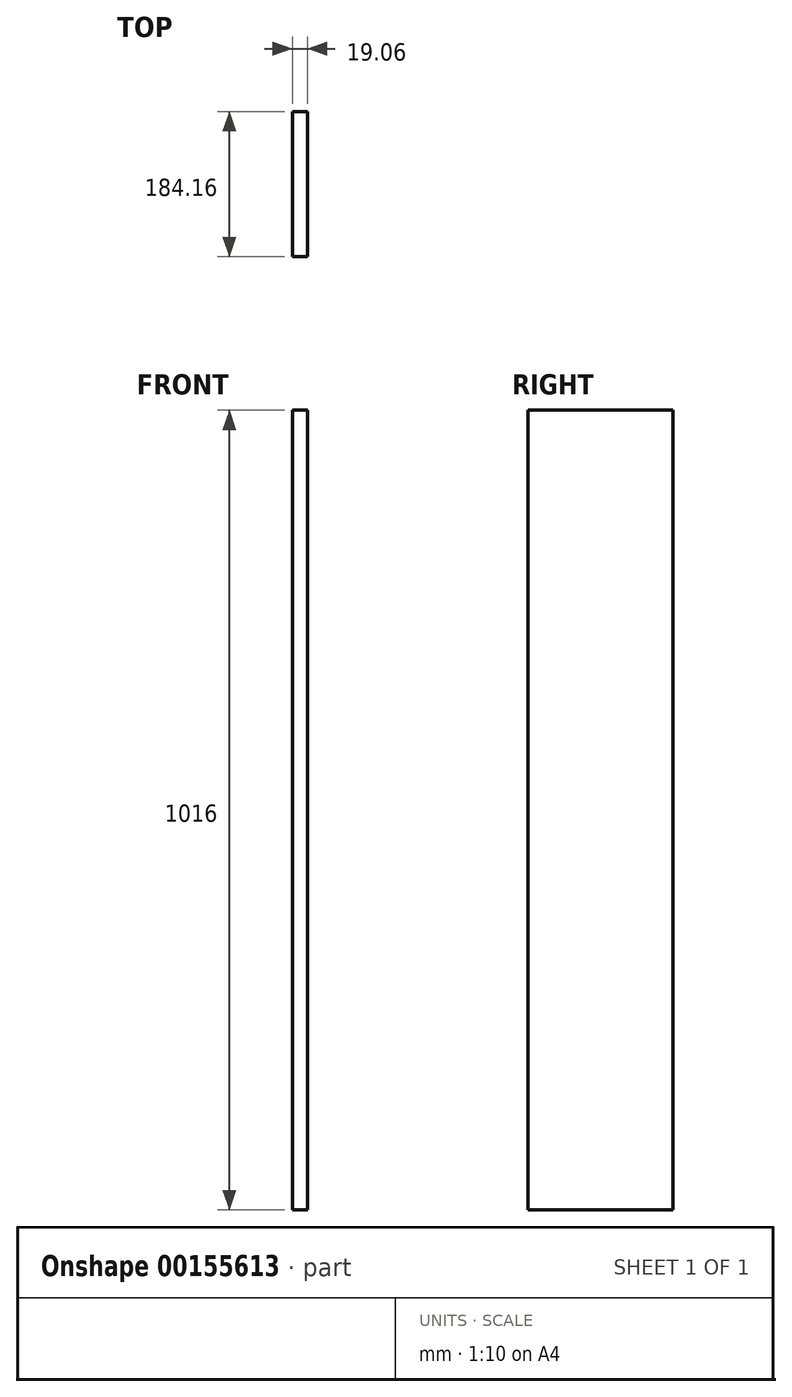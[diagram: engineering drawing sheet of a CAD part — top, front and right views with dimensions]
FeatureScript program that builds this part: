
annotation { "Feature Type Name" : "Feature", "Feature Type Description" : "" }
export const myFeature = defineFeature(function(context is Context, id is Id, definition is map)
    precondition{}
    {
        {
            var Q0;
            Q0=qCreatedBy(makeId("Top.planeOp"),FACE);
            var sketch = newSketch(context, id + "F0", { "sketchPlane" : qUnion([Q0])});
            skLineSegment(sketch, "E0.bottom", {"start": v(-9.53, 92.08) * mm, "end": v(9.52, 92.08) * mm});
            skLineSegment(sketch, "E0.top", {"start": v(-9.53, -92.08) * mm, "end": v(9.52, -92.08) * mm});
            skLineSegment(sketch, "E0.left", {"start": v(-9.53, 92.07) * mm, "end": v(-9.53, -92.08) * mm});
            skLineSegment(sketch, "E0.right", {"start": v(9.52, 92.07) * mm, "end": v(9.52, -92.08) * mm});
            skPoint(sketch, "E0.middle", {"position": v(0, 0) * mm});
            skSolve(sketch);
        }
        {
            var Q0;
            Q0=makeQuery(id+"F0.imprint","IMPRINT",FACE,{"disambiguationData":[TD([[makeQuery(id+"F0.imprint","IMPRINT",EDGE,{"derivedFrom":sQuery(id+"F0.wireOp",EDGE,"E0.bottom")}),-1.0]])]});
            extrude(context, id + "F1", {"entities" : qUnion([Q0]), "depth" : 1016 * mm});
        }
    });
